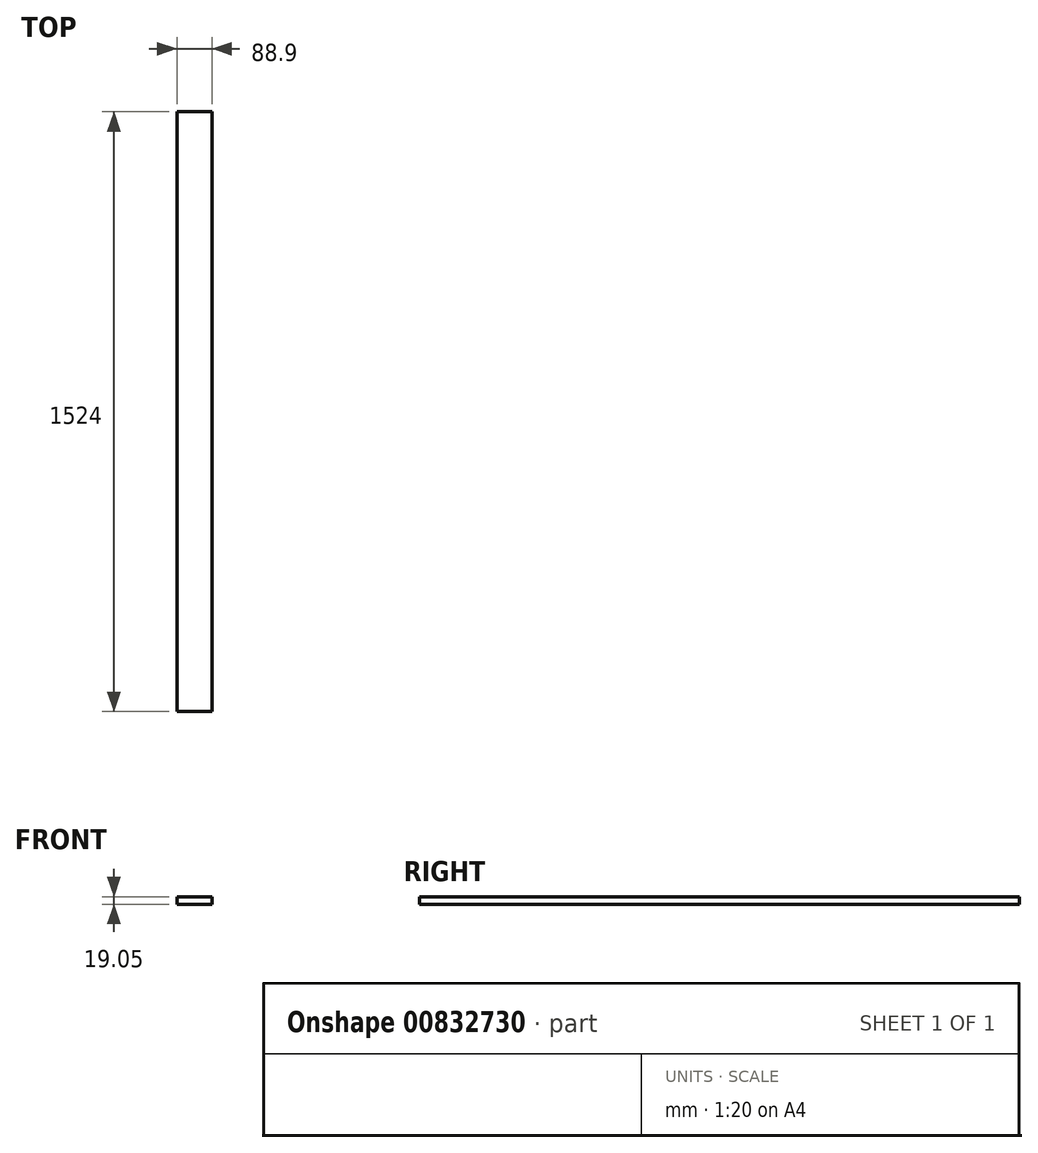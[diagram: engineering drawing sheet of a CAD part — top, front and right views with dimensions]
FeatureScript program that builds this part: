
annotation { "Feature Type Name" : "Feature", "Feature Type Description" : "" }
export const myFeature = defineFeature(function(context is Context, id is Id, definition is map)
    precondition{}
    {
        {
            var Q0;
            Q0=qCreatedBy(makeId("Front.planeOp"),FACE);
            var sketch = newSketch(context, id + "F0", { "sketchPlane" : qUnion([Q0])});
            skLineSegment(sketch, "E0.bottom", {"start": v(0, 0) * mm, "end": v(88.9, 0) * mm});
            skLineSegment(sketch, "E0.top", {"start": v(0, 19.05) * mm, "end": v(88.9, 19.05) * mm});
            skLineSegment(sketch, "E0.left", {"start": v(0, 0) * mm, "end": v(0, 19.05) * mm});
            skLineSegment(sketch, "E0.right", {"start": v(88.9, 0) * mm, "end": v(88.9, 19.05) * mm});
            skSolve(sketch);
        }
        {
            var Q0;
            Q0=makeQuery(id+"F0.imprint","IMPRINT",FACE,{"disambiguationData":[TD([[makeQuery(id+"F0.imprint","IMPRINT",EDGE,{"derivedFrom":sQuery(id+"F0.wireOp",EDGE,"E0.bottom")}),1.0]])]});
            extrude(context, id + "F1", {"entities" : qUnion([Q0]), "oppositeDirection" : true, "depth" : 1524 * mm, "offsetDistance" : 25.4 * mm});
        }
    });
